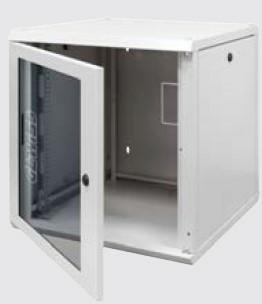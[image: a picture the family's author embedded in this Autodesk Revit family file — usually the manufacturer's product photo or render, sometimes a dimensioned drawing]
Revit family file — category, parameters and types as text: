
# Revit family: Domotics-NetworkCabling-GEWISS-CABINETS_WALL-MOUNTED_19_9U_D400
name_source: partatom
category: Apparecchi elettrici
units: mm (PartAtom-declared; Revit-internal decimal feet)

## family parameters
Condiviso = No
Host = Superficie
Mantenere orientamento annotazione = Sì
Punto di calcolo locali = Sì
Quota connettore circolare = Usa diametro
Taglio con vuoti quando caricato = No
Tipo di parte = Normale

## types (1)
- GW38407 - WALL CABINET 19 9U DEPTH 400MM.
    Cabling unity = 9U
    Catalogue = DOMOTICS
    Category = 19â€ wall-mount cabinet
    Colour = Grey (RAL 7035)
    Depth (mm) = 400 mm
    Descrizione = WALL CABINET 19 9U DEPTH 400MM.
    Door opening = 180°
    Electrocod = 3752
    Finishing = Textured
    IDF = 86af9bb8-2e1d-47f8-8fba-1ee325dc55c9
    IDT = ea368ef7b3c0440fbd5b55759d12ab1b
    IP degree = IP20
    Immagine tipo = B.jpg
    Material = Steel
    Modello = GW38407
    No. uprights = 2
    Outer dim. LxHxD (mm) = 600x470x400
    Produttore = GEWISS S.p.A.
    Prospetto di default = 1219 mm
    SEO = Board
    Static load capacity = 50KG
    Technical sheet = https://www.gewiss.com
    Type of door = Reversible
    URL = https://www.gewiss.com
    Version file RFA = 21.2

## geometry (parser evidence)
native form markers: Sweep x3
no freeform markers — native parametric forms only
